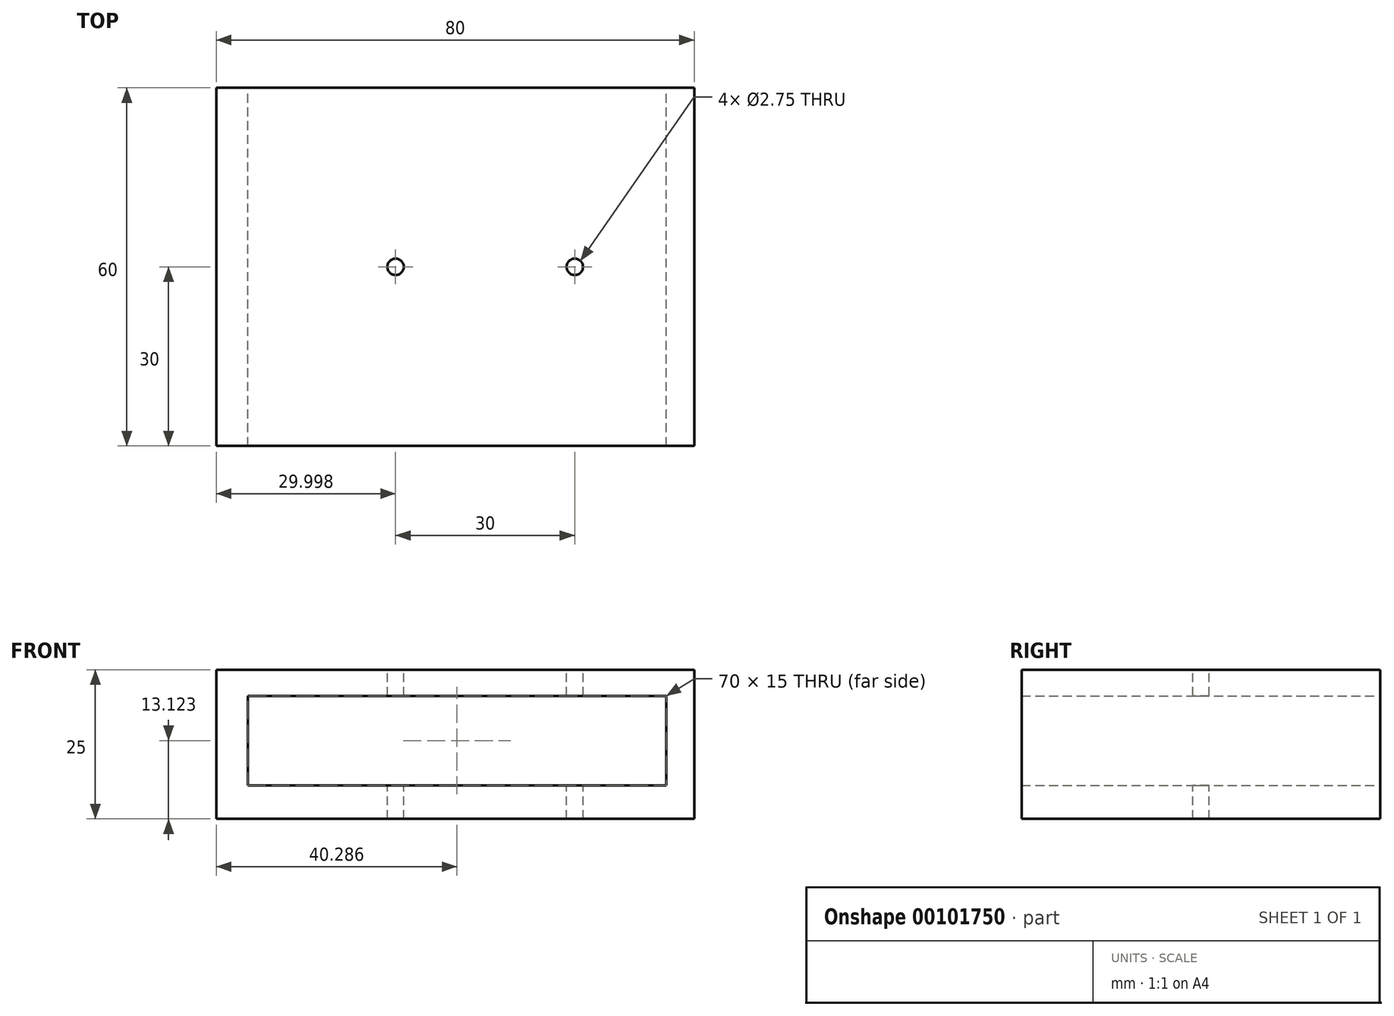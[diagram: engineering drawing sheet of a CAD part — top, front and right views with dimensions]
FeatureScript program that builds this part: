
annotation { "Feature Type Name" : "Feature", "Feature Type Description" : "" }
export const myFeature = defineFeature(function(context is Context, id is Id, definition is map)
    precondition{}
    {
        {
            var Q0;
            Q0=qCreatedBy(makeId("Top.planeOp"),FACE);
            var sketch = newSketch(context, id + "F0", { "sketchPlane" : qUnion([Q0])});
            skLineSegment(sketch, "E0.bottom", {"start": v(-20.97, 36.17) * mm, "end": v(59.03, 36.17) * mm});
            skLineSegment(sketch, "E0.top", {"start": v(-20.97, -23.83) * mm, "end": v(59.03, -23.83) * mm});
            skLineSegment(sketch, "E0.left", {"start": v(-20.97, 36.17) * mm, "end": v(-20.97, -23.83) * mm});
            skLineSegment(sketch, "E0.right", {"start": v(59.03, 36.17) * mm, "end": v(59.03, -23.83) * mm});
            skSolve(sketch);
        }
        {
            var Q0;
            Q0=qSketchRegion(id+"F0",true);
            extrude(context, id + "F1", {"entities" : qUnion([Q0]), "depth" : 25 * mm});
        }
        {
            var Q0;
            Q0=makeQuery(id+"F1.opExtrude","SWEPT_FACE",FACE,{"disambiguationData":[OSD([sQuery(id+"F0.wireOp",EDGE,"E0.bottom")])]});
            var sketch = newSketch(context, id + "F2", { "sketchPlane" : qUnion([Q0])});
            skLineSegment(sketch, "E1.bottom", {"start": v(15.68, 20.62) * mm, "end": v(-54.32, 20.62) * mm});
            skLineSegment(sketch, "E1.top", {"start": v(15.68, 5.62) * mm, "end": v(-54.32, 5.62) * mm});
            skLineSegment(sketch, "E1.left", {"start": v(15.68, 20.62) * mm, "end": v(15.68, 5.62) * mm});
            skLineSegment(sketch, "E1.right", {"start": v(-54.32, 20.62) * mm, "end": v(-54.32, 5.62) * mm});
            skSolve(sketch);
        }
        {
            var Q0;
            Q0=qSketchRegion(id+"F2",true);
            extrude(context, id + "F3", {"entities" : qUnion([Q0]), "operationType" : NewBodyOperationType.REMOVE, "endBound" : BoundingType.THROUGH_ALL, "oppositeDirection" : true, "depth" : 50 * mm});
        }
        {
            var Q0;
            Q0=makeQuery(id+"F1.opExtrude","CAP_FACE",FACE,{"disambiguationData":[OSD([sQuery(id+"F0.wireOp",EDGE,"E0.bottom"),sQuery(id+"F0.wireOp",EDGE,"E0.top"),sQuery(id+"F0.wireOp",EDGE,"E0.left"),sQuery(id+"F0.wireOp",EDGE,"E0.right")])],"isStart":false});
            var sketch = newSketch(context, id + "F4", { "sketchPlane" : qUnion([Q0])});
            skCircle(sketch, "E2", {"center": v(3.89, -54.58) * mm, "radius": 1.38 * mm});
            skCircle(sketch, "E3", {"center": v(99.86, -32.16) * mm, "radius": 1.38 * mm});
            skLineSegment(sketch, "E4", {"start": v(-20.97, 6.17) * mm, "end": v(9.03, 6.17) * mm});
            skLineSegment(sketch, "E5", {"start": v(59.03, 6.17) * mm, "end": v(39.03, 6.17) * mm});
            skPoint(sketch, "E6", {"position": v(9.03, 6.17) * mm});
            skPoint(sketch, "E7", {"position": v(39.03, 6.17) * mm});
            skCircle(sketch, "E8", {"center": v(9.03, 6.17) * mm, "radius": 1.38 * mm});
            skCircle(sketch, "E9", {"center": v(39.03, 6.17) * mm, "radius": 1.38 * mm});
            skSolve(sketch);
        }
        {
            var Q0;
            Q0=makeQuery(id+"F4.imprint","IMPRINT",FACE,{"disambiguationData":[TD([[makeQuery(id+"F4.imprint","IMPRINT",EDGE,{"derivedFrom":sQuery(id+"F4.wireOp",EDGE,"E8")}),1.0]])]});
            var Q1;
            Q1=makeQuery(id+"F4.imprint","IMPRINT",FACE,{"disambiguationData":[TD([[makeQuery(id+"F4.imprint","IMPRINT",EDGE,{"derivedFrom":sQuery(id+"F4.wireOp",EDGE,"E9")}),1.0]])]});
            extrude(context, id + "F5", {"entities" : qUnion([Q0, Q1]), "operationType" : NewBodyOperationType.REMOVE, "endBound" : BoundingType.THROUGH_ALL, "oppositeDirection" : true, "depth" : 25 * mm});
        }
    });
